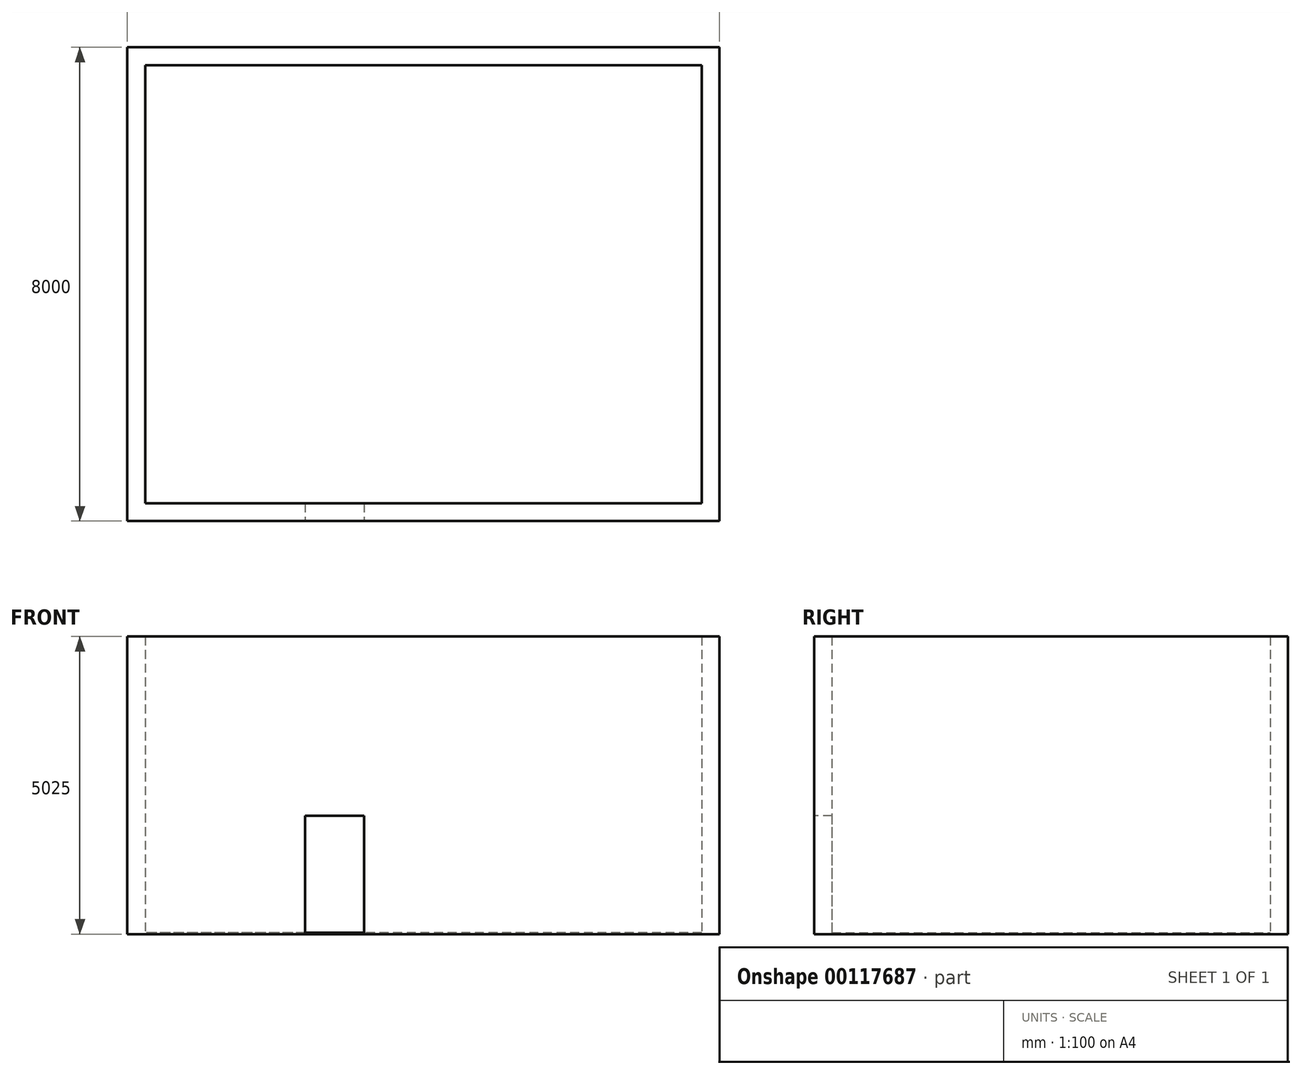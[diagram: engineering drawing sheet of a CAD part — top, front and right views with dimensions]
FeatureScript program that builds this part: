
annotation { "Feature Type Name" : "Feature", "Feature Type Description" : "" }
export const myFeature = defineFeature(function(context is Context, id is Id, definition is map)
    precondition{}
    {
        {
            var Q0;
            Q0=qCreatedBy(makeId("Top.planeOp"),FACE);
            var sketch = newSketch(context, id + "F0", { "sketchPlane" : qUnion([Q0])});
            skLineSegment(sketch, "E0.bottom", {"start": v(5000, -4000) * mm, "end": v(-5000, -4000) * mm});
            skLineSegment(sketch, "E0.top", {"start": v(5000, 4000) * mm, "end": v(-5000, 4000) * mm});
            skLineSegment(sketch, "E0.left", {"start": v(5000, -4000) * mm, "end": v(5000, 4000) * mm});
            skLineSegment(sketch, "E0.right", {"start": v(-5000, -4000) * mm, "end": v(-5000, 4000) * mm});
            skPoint(sketch, "E0.middle", {"position": v(0, 0) * mm});
            skSolve(sketch);
        }
        {
            var Q0;
            Q0=makeQuery(id+"F0.imprint","IMPRINT",FACE,{"disambiguationData":[TD([[makeQuery(id+"F0.imprint","IMPRINT",EDGE,{"derivedFrom":sQuery(id+"F0.wireOp",EDGE,"E0.bottom")}),-1.0]])]});
            extrude(context, id + "F1", {"entities" : qUnion([Q0]), "depth" : 25 * mm});
        }
        {
            var Q0;
            Q0=makeQuery(id+"F1.opExtrude","CAP_FACE",FACE,{"disambiguationData":[OSD([sQuery(id+"F0.wireOp",EDGE,"E0.bottom"),sQuery(id+"F0.wireOp",EDGE,"E0.top"),sQuery(id+"F0.wireOp",EDGE,"E0.left"),sQuery(id+"F0.wireOp",EDGE,"E0.right")])],"isStart":false});
            var sketch = newSketch(context, id + "F2", { "sketchPlane" : qUnion([Q0])});
            skLineSegment(sketch, "E1.bottom", {"start": v(4700, -3700) * mm, "end": v(-4700, -3700) * mm});
            skLineSegment(sketch, "E1.top", {"start": v(4700, 3700) * mm, "end": v(-4700, 3700) * mm});
            skLineSegment(sketch, "E1.left", {"start": v(4700, -3700) * mm, "end": v(4700, 3700) * mm});
            skLineSegment(sketch, "E1.right", {"start": v(-4700, -3700) * mm, "end": v(-4700, 3700) * mm});
            skPoint(sketch, "E1.middle", {"position": v(0, 0) * mm});
            skSolve(sketch);
        }
        {
            var Q0;
            Q0=makeQuery(id+"F2.imprint","IMPRINT",FACE,{"disambiguationData":[TD([[makeQuery(id+"F2.imprint","IMPRINT",EDGE,{"derivedFrom":sQuery(id+"F2.wireOp",EDGE,"E1.bottom")}),1.0]])]});
            extrude(context, id + "F3", {"entities" : qUnion([Q0]), "operationType" : NewBodyOperationType.ADD, "depth" : 5000 * mm});
        }
        {
            var Q0;
            {var subQ0=sQuery(id+"F0.wireOp",EDGE,"E0.bottom");Q0=makeQuery(id+"F3.boolean.opBoolean","MERGE",FACE,{"derivedFrom":[makeQuery(id+"F1.opExtrude","SWEPT_FACE",FACE,{"disambiguationData":[OSD([subQ0])]}),makeQuery(id+"F3.opExtrude","SWEPT_FACE",FACE,{"disambiguationData":[OSD([subQ0])]})]});}
            var sketch = newSketch(context, id + "F4", { "sketchPlane" : qUnion([Q0])});
            skLineSegment(sketch, "E2.bottom", {"start": v(-2000, 0) * mm, "end": v(-1000, 0) * mm});
            skLineSegment(sketch, "E2.top", {"start": v(-2000, 2000) * mm, "end": v(-1000, 2000) * mm});
            skLineSegment(sketch, "E2.left", {"start": v(-2000, 0) * mm, "end": v(-2000, 2000) * mm});
            skLineSegment(sketch, "E2.right", {"start": v(-1000, 0) * mm, "end": v(-1000, 2000) * mm});
            skSolve(sketch);
        }
        {
            var Q0;
            Q0=makeQuery(id+"F4.imprint","IMPRINT",FACE,{"disambiguationData":[TD([[makeQuery(id+"F4.imprint","IMPRINT",EDGE,{"derivedFrom":sQuery(id+"F4.wireOp",EDGE,"E2.bottom")}),-1.0]])]});
            var Q1;
            Q1=makeQuery(id+"F3.opExtrude","SWEPT_FACE",FACE,{"disambiguationData":[OSD([sQuery(id+"F2.wireOp",EDGE,"E1.bottom")])]});
            extrude(context, id + "F5", {"entities" : qUnion([Q0]), "operationType" : NewBodyOperationType.REMOVE, "endBound" : BoundingType.UP_TO_SURFACE, "oppositeDirection" : true, "endBoundEntityFace" : qUnion([Q1]), "depth" : 25 * mm});
        }
    });
